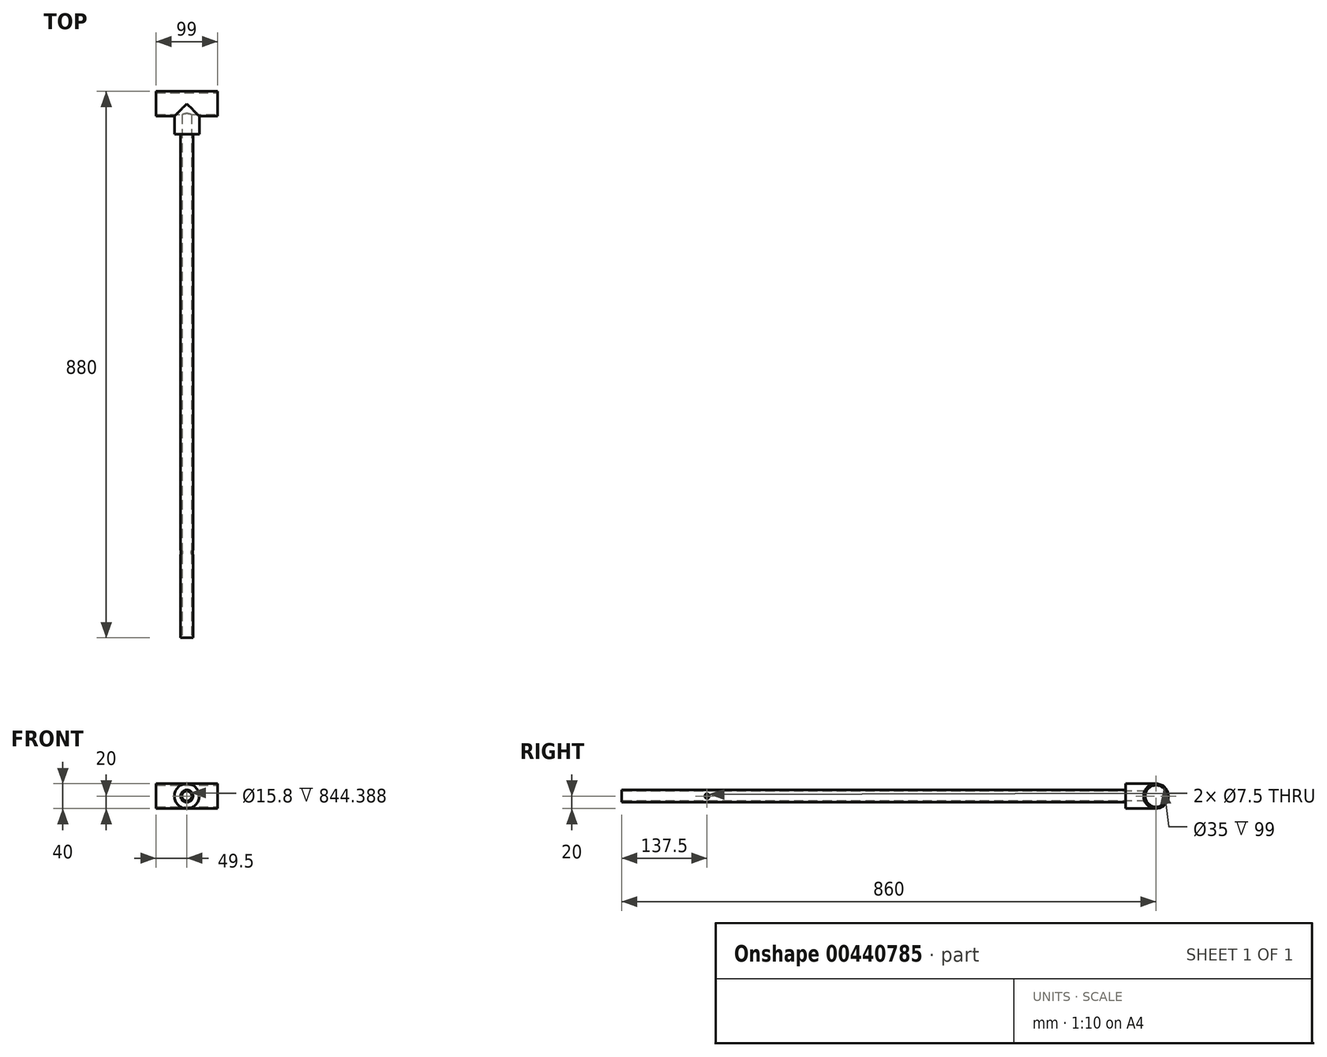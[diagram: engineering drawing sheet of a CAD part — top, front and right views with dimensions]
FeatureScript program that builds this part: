
annotation { "Feature Type Name" : "Feature", "Feature Type Description" : "" }
export const myFeature = defineFeature(function(context is Context, id is Id, definition is map)
    precondition{}
    {
        {
            var Q0;
            Q0=qCreatedBy(makeId("Front.planeOp"),FACE);
            var sketch = newSketch(context, id + "F0", { "sketchPlane" : qUnion([Q0])});
            skCircle(sketch, "E0", {"center": v(0, 0) * mm, "radius": 10 * mm});
            skSolve(sketch);
        }
        {
            var Q0;
            Q0=makeQuery(id+"F0.imprint","IMPRINT",FACE,{"disambiguationData":[TD([[makeQuery(id+"F0.imprint","IMPRINT",EDGE,{"derivedFrom":sQuery(id+"F0.wireOp",EDGE,"E0")}),1.0]])]});
            extrude(context, id + "F1", {"entities" : qUnion([Q0]), "depth" : 860 * mm});
        }
        {
            var Q0;
            Q0=qCreatedBy(makeId("Right.planeOp"),FACE);
            var sketch = newSketch(context, id + "F2", { "sketchPlane" : qUnion([Q0])});
            skCircle(sketch, "E1", {"center": v(0, 0) * mm, "radius": 20 * mm});
            skSolve(sketch);
        }
        {
            var Q0;
            Q0=makeQuery(id+"F2.imprint","IMPRINT",FACE,{"disambiguationData":[TD([[makeQuery(id+"F2.imprint","IMPRINT",EDGE,{"derivedFrom":sQuery(id+"F2.wireOp",EDGE,"E1")}),1.0]])]});
            extrude(context, id + "F3", {"entities" : qUnion([Q0]), "operationType" : NewBodyOperationType.ADD, "endBound" : BoundingType.SYMMETRIC, "depth" : 99 * mm});
        }
        {
            var Q0;
            Q0=qCreatedBy(makeId("Right.planeOp"),FACE);
            var sketch = newSketch(context, id + "F4", { "sketchPlane" : qUnion([Q0])});
            skCircle(sketch, "E2", {"center": v(-722.5, 0) * mm, "radius": 3.75 * mm});
            skSolve(sketch);
        }
        {
            var Q0;
            Q0 = qSketchRegion(id + "F4", true);
            extrude(context, id + "F5", {"entities" : qUnion([Q0]), "operationType" : NewBodyOperationType.REMOVE, "depth" : 96 * mm, "hasSecondDirection" : true, "secondDirectionOppositeDirection" : true, "secondDirectionDepth" : 63 * mm});
        }
        {
            var Q0;
            Q0=makeQuery(id+"F3.opExtrude","CAP_FACE",FACE,{"disambiguationData":[OSD([sQuery(id+"F2.wireOp",EDGE,"E1")])],"isStart":false});
            var sketch = newSketch(context, id + "F6", { "sketchPlane" : qUnion([Q0])});
            skCircle(sketch, "E3", {"center": v(0, 0) * mm, "radius": 17.5 * mm});
            skSolve(sketch);
        }
        {
            var Q0;
            Q0=makeQuery(id+"F6.imprint","IMPRINT",FACE,{"disambiguationData":[TD([[makeQuery(id+"F6.imprint","IMPRINT",EDGE,{"derivedFrom":sQuery(id+"F6.wireOp",EDGE,"E3")}),1.0]])]});
            extrude(context, id + "F7", {"entities" : qUnion([Q0]), "operationType" : NewBodyOperationType.REMOVE, "endBound" : BoundingType.SYMMETRIC, "oppositeDirection" : true, "depth" : 432 * mm});
        }
        {
            var Q0;
            Q0=makeQuery(id+"F1.opExtrude","CAP_FACE",FACE,{"disambiguationData":[OSD([sQuery(id+"F0.wireOp",EDGE,"E0")])],"isStart":false});
            var sketch = newSketch(context, id + "F8", { "sketchPlane" : qUnion([Q0])});
            skCircle(sketch, "E4", {"center": v(0, 0) * mm, "radius": 7.9 * mm});
            skSolve(sketch);
        }
        {
            var Q0;
            Q0=makeQuery(id+"F8.imprint","IMPRINT",FACE,{"disambiguationData":[TD([[makeQuery(id+"F8.imprint","IMPRINT",EDGE,{"derivedFrom":sQuery(id+"F8.wireOp",EDGE,"E4")}),1.0]])]});
            extrude(context, id + "F9", {"entities" : qUnion([Q0]), "operationType" : NewBodyOperationType.REMOVE, "oppositeDirection" : true, "depth" : 850 * mm});
        }
        {
            var Q0;
            Q0=qCreatedBy(makeId("Front.planeOp"),FACE);
            var sketch = newSketch(context, id + "F10", { "sketchPlane" : qUnion([Q0])});
            skCircle(sketch, "E5", {"center": v(0, 0) * mm, "radius": 20 * mm});
            skCircle(sketch, "E6", {"center": v(0, 0) * mm, "radius": 10 * mm});
            skSolve(sketch);
        }
        {
            var Q0;
            Q0 = qSketchRegion(id + "F10", true);
            extrude(context, id + "F11", {"entities" : qUnion([Q0]), "operationType" : NewBodyOperationType.ADD, "depth" : 49 * mm});
        }
        {
            var Q0;
            Q0=makeQuery(id+"F3.opExtrude","CAP_FACE",FACE,{"disambiguationData":[OSD([sQuery(id+"F2.wireOp",EDGE,"E1")])],"isStart":false});
            var sketch = newSketch(context, id + "F12", { "sketchPlane" : qUnion([Q0])});
            skCircle(sketch, "E7", {"center": v(0, 0) * mm, "radius": 17.5 * mm});
            skSolve(sketch);
        }
        {
            var Q0;
            Q0=makeQuery(id+"F12.imprint","IMPRINT",FACE,{"disambiguationData":[TD([[makeQuery(id+"F12.imprint","IMPRINT",EDGE,{"derivedFrom":sQuery(id+"F12.wireOp",EDGE,"E7")}),1.0]])]});
            extrude(context, id + "F13", {"entities" : qUnion([Q0]), "operationType" : NewBodyOperationType.REMOVE, "oppositeDirection" : true, "depth" : 133 * mm});
        }
    });
